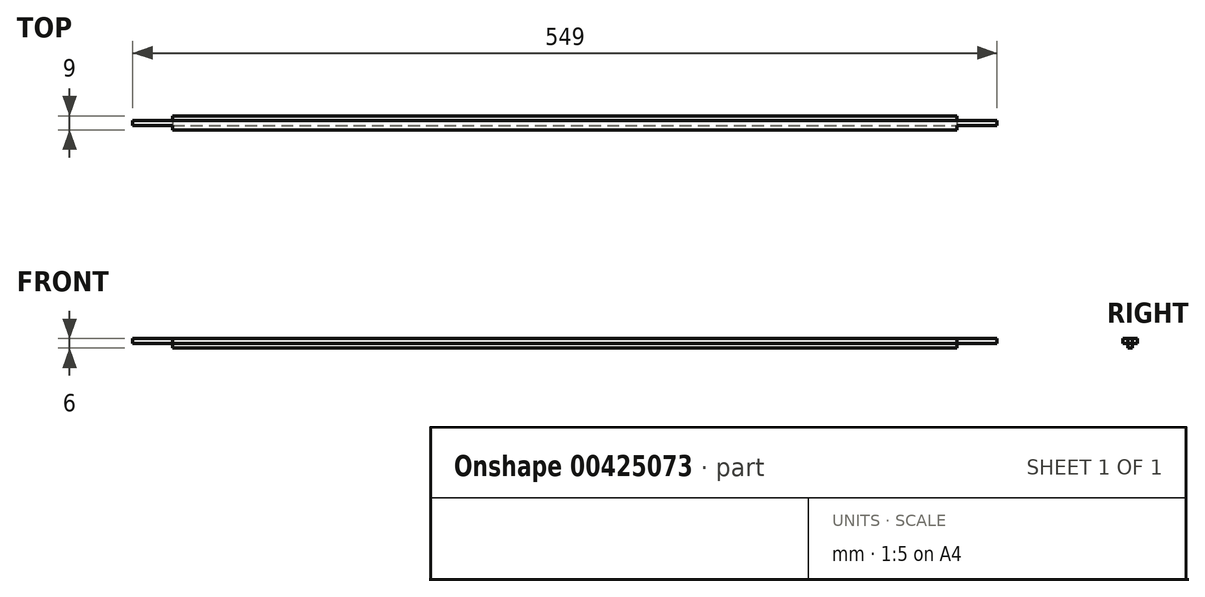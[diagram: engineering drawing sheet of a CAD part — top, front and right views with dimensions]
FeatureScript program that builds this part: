
annotation { "Feature Type Name" : "Feature", "Feature Type Description" : "" }
export const myFeature = defineFeature(function(context is Context, id is Id, definition is map)
    precondition{}
    {
        {
            var Q0;
            Q0=qCreatedBy(makeId("Top.planeOp"),FACE);
            var sketch = newSketch(context, id + "F0", { "sketchPlane" : qUnion([Q0])});
            skLineSegment(sketch, "E0.bottom", {"start": v(-318.53, -149.4) * mm, "end": v(230.47, -149.4) * mm});
            skLineSegment(sketch, "E0.top", {"start": v(-318.53, -152.4) * mm, "end": v(230.47, -152.4) * mm});
            skLineSegment(sketch, "E0.left", {"start": v(-318.53, -149.4) * mm, "end": v(-318.53, -152.4) * mm});
            skLineSegment(sketch, "E0.right", {"start": v(230.47, -149.4) * mm, "end": v(230.47, -152.4) * mm});
            skSolve(sketch);
        }
        {
            var Q0;
            Q0 = qSketchRegion(id + "F0", true);
            extrude(context, id + "F1", {"entities" : qUnion([Q0]), "depth" : 3 * mm});
        }
        {
            var Q0;
            Q0=qCreatedBy(makeId("Top.planeOp"),FACE);
            var sketch = newSketch(context, id + "F2", { "sketchPlane" : qUnion([Q0])});
            skLineSegment(sketch, "E1.bottom", {"start": v(-293.13, -152.4) * mm, "end": v(205.07, -152.4) * mm});
            skLineSegment(sketch, "E1.top", {"start": v(-293.13, -155.4) * mm, "end": v(205.07, -155.4) * mm});
            skLineSegment(sketch, "E1.left", {"start": v(-293.13, -152.4) * mm, "end": v(-293.13, -155.4) * mm});
            skLineSegment(sketch, "E1.right", {"start": v(205.07, -152.4) * mm, "end": v(205.07, -155.4) * mm});
            skSolve(sketch);
        }
        {
            var Q0;
            Q0 = qSketchRegion(id + "F2", true);
            extrude(context, id + "F3", {"entities" : qUnion([Q0]), "operationType" : NewBodyOperationType.ADD, "depth" : 3 * mm});
        }
        {
            var Q0;
            Q0=qCreatedBy(makeId("Top.planeOp"),FACE);
            var sketch = newSketch(context, id + "F4", { "sketchPlane" : qUnion([Q0])});
            skLineSegment(sketch, "E2.bottom", {"start": v(-293.13, -146.4) * mm, "end": v(205.07, -146.4) * mm});
            skLineSegment(sketch, "E2.top", {"start": v(-293.13, -149.4) * mm, "end": v(205.07, -149.4) * mm});
            skLineSegment(sketch, "E2.left", {"start": v(-293.13, -146.4) * mm, "end": v(-293.13, -149.4) * mm});
            skLineSegment(sketch, "E2.right", {"start": v(205.07, -146.4) * mm, "end": v(205.07, -149.4) * mm});
            skSolve(sketch);
        }
        {
            var Q0;
            Q0 = qSketchRegion(id + "F4", true);
            extrude(context, id + "F5", {"entities" : qUnion([Q0]), "depth" : 3 * mm});
        }
        {
            var Q0;
            Q0=qCreatedBy(makeId("Top.planeOp"),FACE);
            var sketch = newSketch(context, id + "F6", { "sketchPlane" : qUnion([Q0])});
            skLineSegment(sketch, "E3.bottom", {"start": v(-293.13, -149.4) * mm, "end": v(205.07, -149.4) * mm});
            skLineSegment(sketch, "E3.top", {"start": v(-293.13, -152.4) * mm, "end": v(205.07, -152.4) * mm});
            skLineSegment(sketch, "E3.left", {"start": v(-293.13, -149.4) * mm, "end": v(-293.13, -152.4) * mm});
            skLineSegment(sketch, "E3.right", {"start": v(205.07, -149.4) * mm, "end": v(205.07, -152.4) * mm});
            skSolve(sketch);
        }
        {
            var Q0;
            Q0 = qSketchRegion(id + "F6", true);
            extrude(context, id + "F7", {"entities" : qUnion([Q0]), "oppositeDirection" : true, "depth" : 3 * mm});
        }
    });
